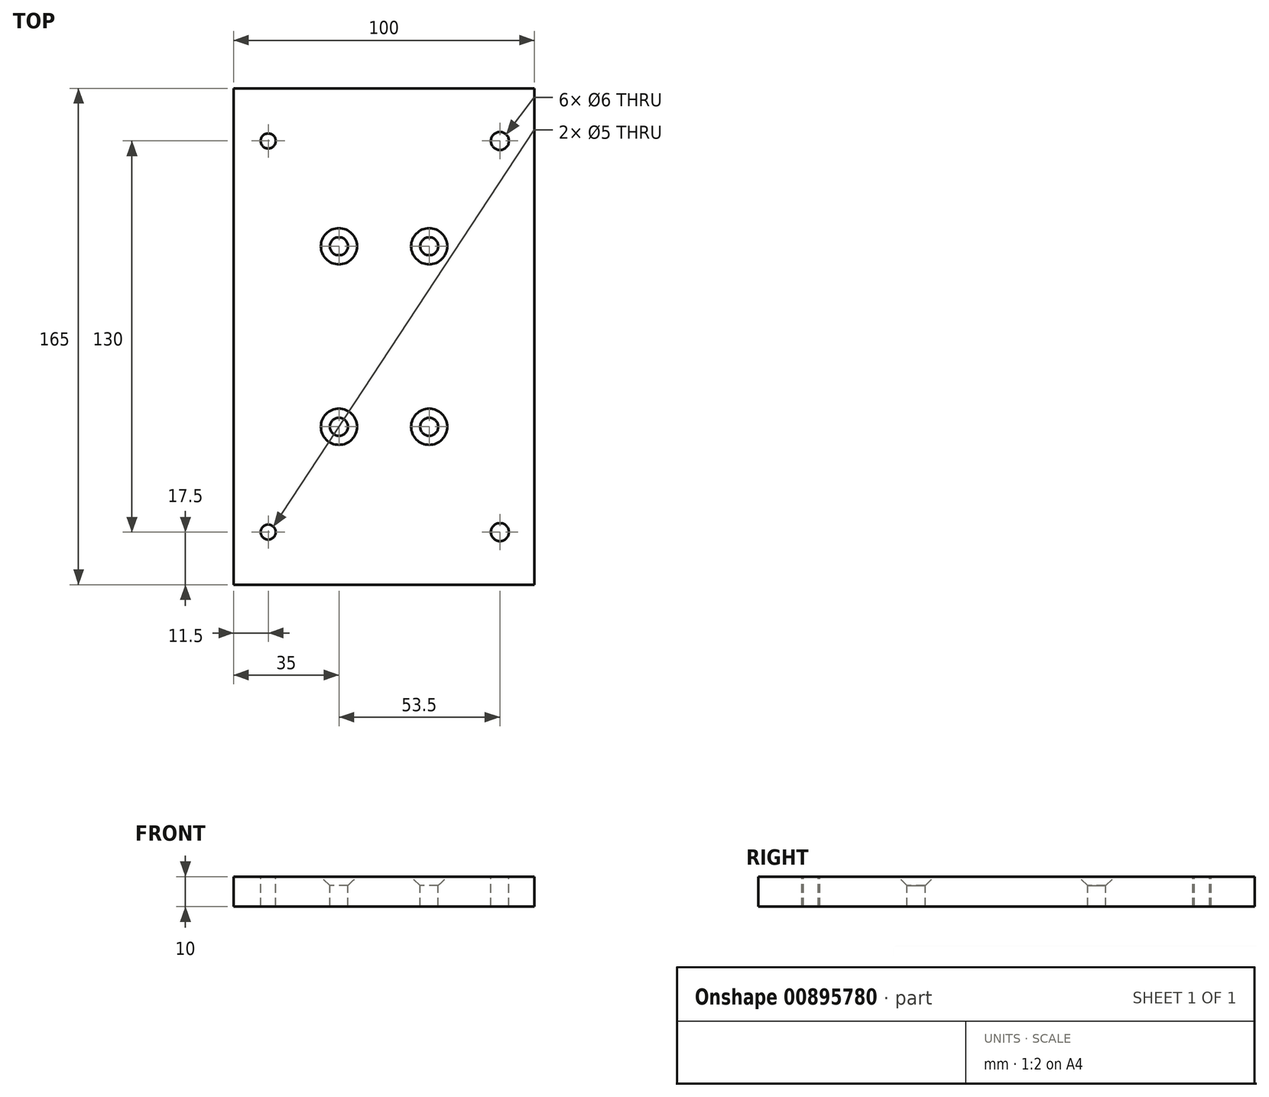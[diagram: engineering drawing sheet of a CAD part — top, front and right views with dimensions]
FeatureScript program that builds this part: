
annotation { "Feature Type Name" : "Feature", "Feature Type Description" : "" }
export const myFeature = defineFeature(function(context is Context, id is Id, definition is map)
    precondition{}
    {
        {
            var Q0;
            Q0=qCreatedBy(makeId("Top.planeOp"),FACE);
            var sketch = newSketch(context, id + "F0", { "sketchPlane" : qUnion([Q0])});
            skLineSegment(sketch, "E0.bottom", {"start": v(-50, 82.5) * mm, "end": v(50, 82.5) * mm});
            skLineSegment(sketch, "E0.top", {"start": v(-50, -82.5) * mm, "end": v(50, -82.5) * mm});
            skLineSegment(sketch, "E0.left", {"start": v(-50, 82.5) * mm, "end": v(-50, -82.5) * mm});
            skLineSegment(sketch, "E0.right", {"start": v(50, 82.5) * mm, "end": v(50, -82.5) * mm});
            skPoint(sketch, "E0.middle", {"position": v(0, 0) * mm});
            skCircle(sketch, "E1", {"center": v(-15, 30) * mm, "radius": 3 * mm});
            skCircle(sketch, "E2", {"center": v(15, 30) * mm, "radius": 3 * mm});
            skCircle(sketch, "E3.MirrorC", {"center": v(15, -30) * mm, "radius": 3 * mm});
            skCircle(sketch, "E4.MirrorC", {"center": v(-15, -30) * mm, "radius": 3 * mm});
            skCircle(sketch, "E5", {"center": v(38.5, 65) * mm, "radius": 2.5 * mm});
            skCircle(sketch, "E6.MirrorC", {"center": v(38.5, -65) * mm, "radius": 2.5 * mm});
            skCircle(sketch, "E7.MirrorC", {"center": v(-38.5, -65) * mm, "radius": 2.5 * mm});
            skCircle(sketch, "E8.MirrorC", {"center": v(-38.5, 65) * mm, "radius": 2.5 * mm});
            skSolve(sketch);
        }
        {
            var Q0;
            Q0=qSketchRegion(id+"F0",true);
            var Q1;
            Q1=makeQuery(id+"F0.imprint","IMPRINT",FACE,{"disambiguationData":[TD([[makeQuery(id+"F0.imprint","IMPRINT",EDGE,{"derivedFrom":sQuery(id+"F0.wireOp",EDGE,"E1")}),1.0]])]});
            var Q2;
            Q2=makeQuery(id+"F0.imprint","IMPRINT",FACE,{"disambiguationData":[TD([[makeQuery(id+"F0.imprint","IMPRINT",EDGE,{"derivedFrom":sQuery(id+"F0.wireOp",EDGE,"E4.MirrorC")}),-1.0]])]});
            var Q3;
            Q3=makeQuery(id+"F0.imprint","IMPRINT",FACE,{"disambiguationData":[TD([[makeQuery(id+"F0.imprint","IMPRINT",EDGE,{"derivedFrom":sQuery(id+"F0.wireOp",EDGE,"E3.MirrorC")}),-1.0]])]});
            var Q4;
            Q4=makeQuery(id+"F0.imprint","IMPRINT",FACE,{"disambiguationData":[TD([[makeQuery(id+"F0.imprint","IMPRINT",EDGE,{"derivedFrom":sQuery(id+"F0.wireOp",EDGE,"E6.MirrorC")}),-1.0]])]});
            var Q5;
            Q5=makeQuery(id+"F0.imprint","IMPRINT",FACE,{"disambiguationData":[TD([[makeQuery(id+"F0.imprint","IMPRINT",EDGE,{"derivedFrom":sQuery(id+"F0.wireOp",EDGE,"E2")}),1.0]])]});
            var Q6;
            Q6=makeQuery(id+"F0.imprint","IMPRINT",FACE,{"disambiguationData":[TD([[makeQuery(id+"F0.imprint","IMPRINT",EDGE,{"derivedFrom":sQuery(id+"F0.wireOp",EDGE,"E5")}),1.0]])]});
            extrude(context, id + "F1", {"entities" : qUnion([Q0, Q1, Q2, Q3, Q4, Q5, Q6]), "oppositeDirection" : true, "offsetDistance" : 25 * mm, "depth" : 10 * mm});
        }
        {
            var Q0;
            Q0=sQuery(id+"F0.wireOp",VERTEX,"E1.center");
            var Q1;
            Q1=sQuery(id+"F0.wireOp",VERTEX,"E2.center");
            var Q2;
            Q2=sQuery(id+"F0.wireOp",VERTEX,"E4.MirrorC.center");
            var Q3;
            Q3=sQuery(id+"F0.wireOp",VERTEX,"E3.MirrorC.center");
            var Q4;
            Q4=makeQuery(id+"F1.opExtrude","SWEPT_BODY",BODY,{"disambiguationData":[OSD([sQuery(id+"F0.wireOp",EDGE,"E0.bottom"),sQuery(id+"F0.wireOp",EDGE,"E0.top"),sQuery(id+"F0.wireOp",EDGE,"E0.left"),sQuery(id+"F0.wireOp",EDGE,"E0.right")])]});
            hole(context, id + "F2", {"style" : HoleStyle.C_SINK, "endStyle" : HoleEndStyle.THROUGH, "holeDiameter" : 6 * mm, "cSinkDiameter" : 12 * mm, "cSinkAngle" : 90 * degree, "locations" : qUnion([Q0, Q1, Q2, Q3]), "scope" : qUnion([Q4]), "isTappedThrough" : true});
        }
        {
            var Q0;
            Q0=sQuery(id+"F0.wireOp",VERTEX,"E5.center");
            var Q1;
            Q1=sQuery(id+"F0.wireOp",VERTEX,"E6.MirrorC.center");
            var Q2;
            Q2=makeQuery(id+"F1.opExtrude","SWEPT_BODY",BODY,{"disambiguationData":[OSD([sQuery(id+"F0.wireOp",EDGE,"E0.bottom"),sQuery(id+"F0.wireOp",EDGE,"E0.top"),sQuery(id+"F0.wireOp",EDGE,"E0.left"),sQuery(id+"F0.wireOp",EDGE,"E0.right")])]});
            hole(context, id + "F3", {"style" : HoleStyle.SIMPLE, "endStyle" : HoleEndStyle.THROUGH, "holeDiameter" : 6 * mm, "locations" : qUnion([Q0, Q1]), "scope" : qUnion([Q2]), "isTappedThrough" : true});
        }
    });
